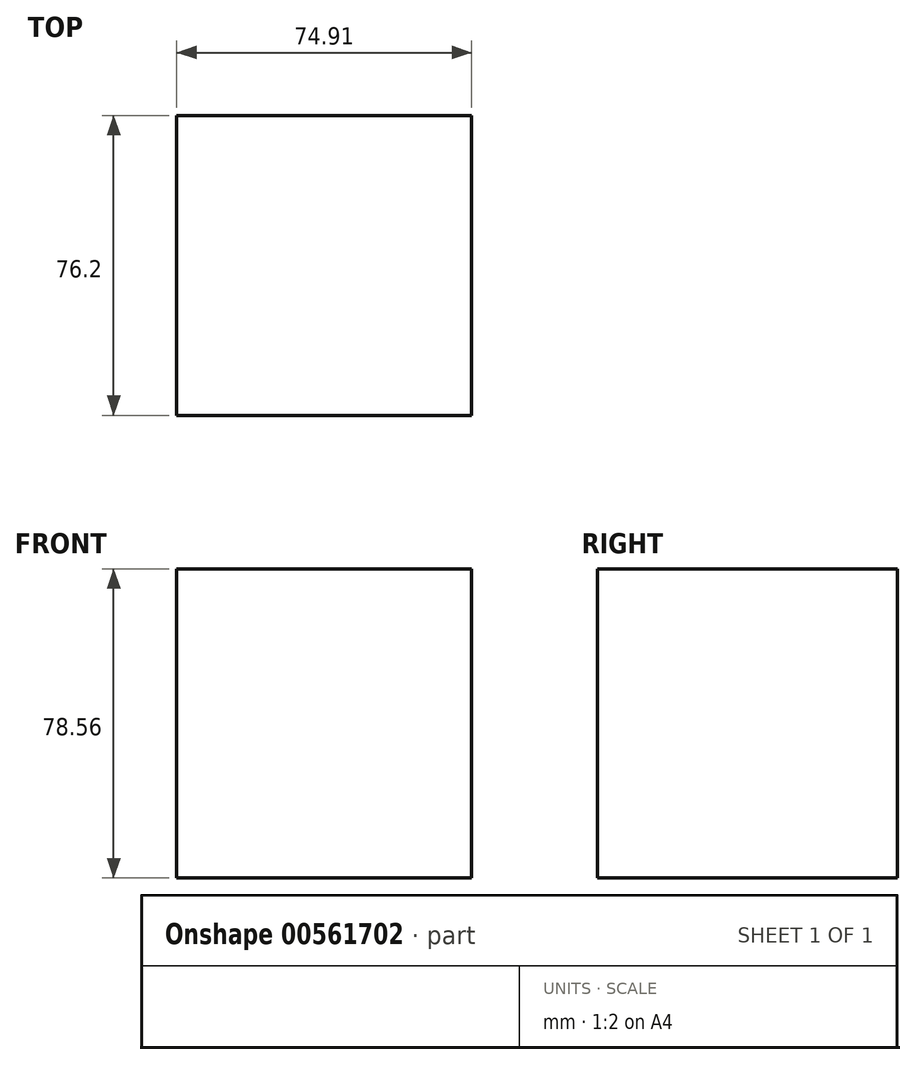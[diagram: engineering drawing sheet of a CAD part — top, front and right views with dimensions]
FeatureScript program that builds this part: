
annotation { "Feature Type Name" : "Feature", "Feature Type Description" : "" }
export const myFeature = defineFeature(function(context is Context, id is Id, definition is map)
    precondition{}
    {
        {
            var Q0;
            Q0=qCreatedBy(makeId("Front.planeOp"),FACE);
            var sketch = newSketch(context, id + "F0", { "sketchPlane" : qUnion([Q0])});
            skLineSegment(sketch, "E0.bottom", {"start": v(0, -3.32) * mm, "end": v(-74.91, -3.32) * mm});
            skLineSegment(sketch, "E0.top", {"start": v(0, 75.24) * mm, "end": v(-74.91, 75.24) * mm});
            skLineSegment(sketch, "E0.left", {"start": v(0, -3.32) * mm, "end": v(0, 75.24) * mm});
            skLineSegment(sketch, "E0.right", {"start": v(-74.91, -3.32) * mm, "end": v(-74.91, 75.24) * mm});
            skSolve(sketch);
        }
        {
            var Q0;
            Q0=makeQuery(id+"F0.imprint","IMPRINT",FACE,{"disambiguationData":[TD([[makeQuery(id+"F0.imprint","IMPRINT",EDGE,{"derivedFrom":sQuery(id+"F0.wireOp",EDGE,"E0.bottom")}),-1.0]])]});
            extrude(context, id + "F1", {"entities" : qUnion([Q0]), "depth" : 76.2 * mm, "offsetDistance" : 25.4 * mm});
        }
    });
